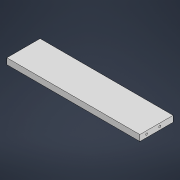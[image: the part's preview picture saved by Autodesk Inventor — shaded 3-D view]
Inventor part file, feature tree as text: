
AUTODESK INVENTOR PART (.ipt)
format: ipt  version: 2021.2 (Build 252289000, 289)  size: 130,048 bytes
history: native  units: mm
features: sketch x4, hole x4, extrude x1
ambient origin geometry x8: Origin, YZ Plane, XZ Plane, XY Plane, X Axis, Y Axis, Z Axis, Center Point
bodies: Solid1 (feature_tree)
feature tree (9):
  extrude  "Extrusion1"  Depth=20.0mm
  sketch  "Sketch2"  dims[d5=40.0mm d7=20.0mm]
  sketch  "Sketch3"  dims[d8=40.0mm]
  hole  "Hole1"  [1 undecoded]
  sketch  "Sketch4"  dims[d9=6.0mm d10=6.0mm d11=4.0mm d12=2.0mm d13=90.0deg d14=30.0mm d15=0.0mm d24=40.0mm d26=20.0mm d27=40.0mm d28=6.0mm d29=6.0mm d30=4.0mm d31=2.0mm d32=90.0deg d33=30.0mm d34=0.0mm d42=15.0mm d43=6.0mm d44=4.0mm d45=2.0mm d46=90.0deg d47=14.0mm d48=0.0mm d56=15.0mm d57=6.0mm d58=4.0mm d59=2.0mm d60=90.0deg d61=14.0mm d62=0.0mm d71=20.0mm d72=30.0mm]
  hole  "Hole3"  [1 undecoded]
  hole  "Hole5"  [1 undecoded]
  hole  "Hole7"  [1 undecoded]
  sketch  "Sketch1"  dims[d3=0.0mm d4=20.0mm]
note: 4 required parameter values undecoded (feature->parameter linkage not recoverable at this tier; creation-order binding heuristic only, values carry confidence <= 0.55)
